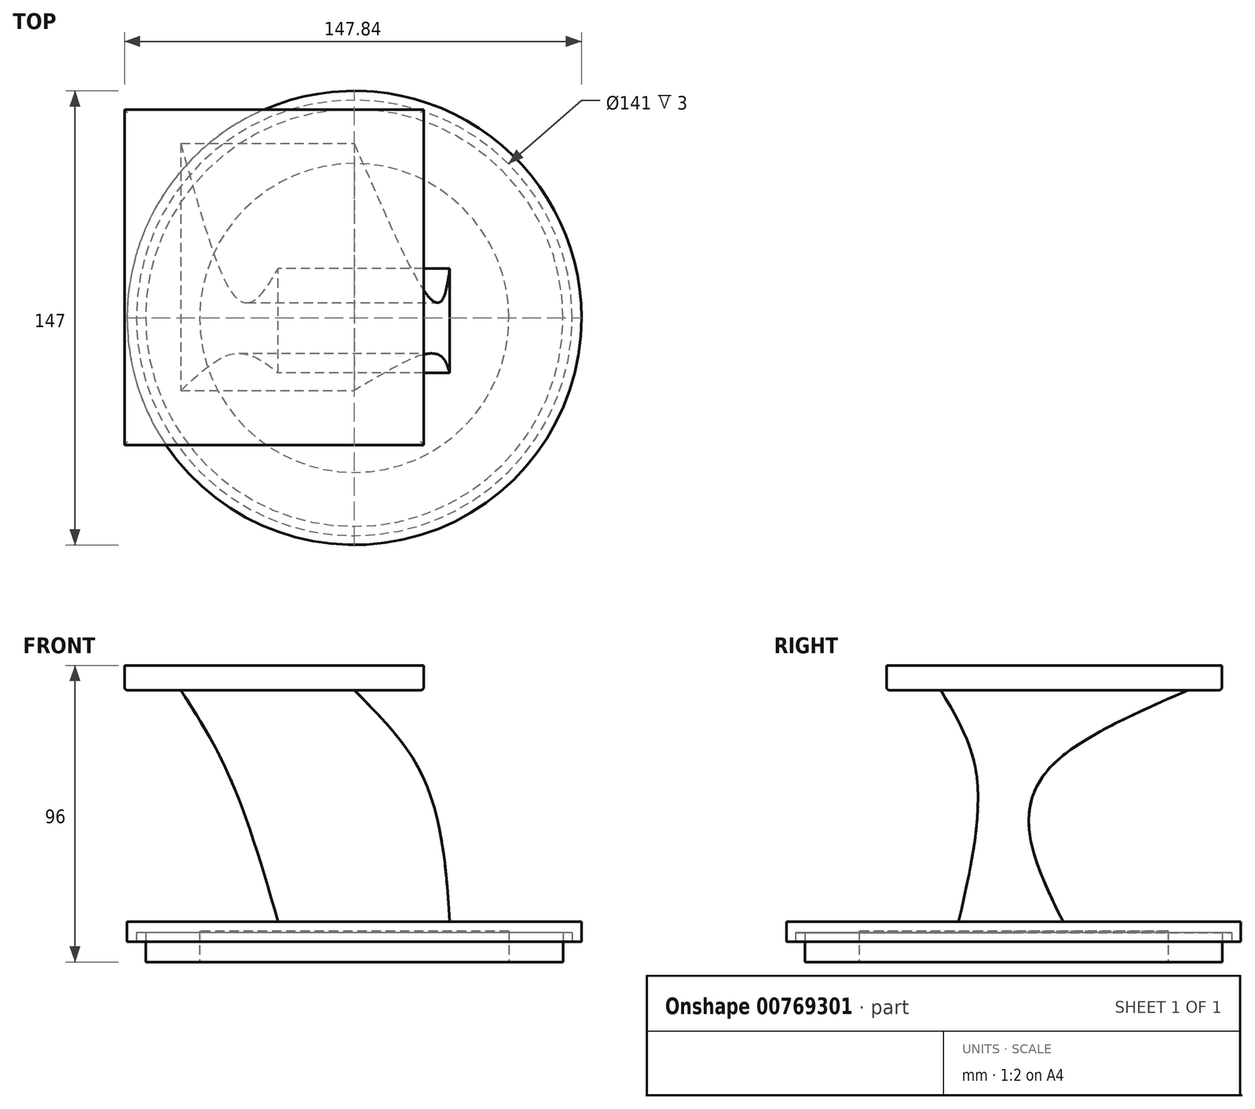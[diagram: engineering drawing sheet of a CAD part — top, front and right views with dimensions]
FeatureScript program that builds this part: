
annotation { "Feature Type Name" : "Feature", "Feature Type Description" : "" }
export const myFeature = defineFeature(function(context is Context, id is Id, definition is map)
    precondition{}
    {
        {
            var Q0;
            Q0=qCreatedBy(makeId("Top.planeOp"),FACE);
            var sketch = newSketch(context, id + "F0", { "sketchPlane" : qUnion([Q0])});
            skCircle(sketch, "E0", {"center": v(0, 0) * mm, "radius": 50 * mm});
            skCircle(sketch, "E1", {"center": v(0, 0) * mm, "radius": 67.5 * mm});
            skCircle(sketch, "E2", {"center": v(0, 0) * mm, "radius": 70.5 * mm});
            skCircle(sketch, "E3", {"center": v(0, 0) * mm, "radius": 73.5 * mm});
            skCircle(sketch, "E4", {"center": v(0, 0) * mm, "radius": 56.9 * mm, "construction": true});
            skPoint(sketch, "E5", {"position": v(56.9, 0) * mm});
            skPoint(sketch, "E6", {"position": v(67.5, 0) * mm});
            skPoint(sketch, "E7", {"position": v(70.5, 0) * mm});
            skPoint(sketch, "E8", {"position": v(73.5, 0) * mm});
            skLineSegment(sketch, "E9", {"start": v(0, 0) * mm, "end": v(0, 56.9) * mm, "construction": true});
            skLineSegment(sketch, "E10", {"start": v(0, 0) * mm, "end": v(-49.28, -28.45) * mm, "construction": true});
            skLineSegment(sketch, "E11", {"start": v(0, 0) * mm, "end": v(49.28, -28.45) * mm, "construction": true});
            skPoint(sketch, "E12", {"position": v(0, 56.9) * mm});
            skPoint(sketch, "E13", {"position": v(-49.28, -28.45) * mm});
            skPoint(sketch, "E14", {"position": v(49.28, -28.45) * mm});
            skPoint(sketch, "E15", {"position": v(0, 73.5) * mm});
            skLineSegment(sketch, "E16", {"start": v(-49.28, -28.45) * mm, "end": v(-63.47, -37.07) * mm, "construction": true});
            skPoint(sketch, "E17", {"position": v(-63.47, -37.07) * mm});
            skLineSegment(sketch, "E18", {"start": v(49.28, -28.45) * mm, "end": v(63.65, -36.75) * mm, "construction": true});
            skPoint(sketch, "E19", {"position": v(63.65, -36.75) * mm});
            skSolve(sketch);
        }
        {
            var Q0;
            Q0=makeQuery(id+"F0.imprint","IMPRINT",FACE,{"disambiguationData":[TD([[makeQuery(id+"F0.imprint","IMPRINT",EDGE,{"derivedFrom":sQuery(id+"F0.wireOp",EDGE,"E2")}),-1.0]])]});
            var Q1;
            Q1=makeQuery(id+"F0.imprint","IMPRINT",FACE,{"disambiguationData":[TD([[makeQuery(id+"F0.imprint","IMPRINT",EDGE,{"derivedFrom":sQuery(id+"F0.wireOp",EDGE,"E0")}),-1.0]])]});
            var Q2;
            Q2=makeQuery(id+"F0.imprint","IMPRINT",FACE,{"disambiguationData":[TD([[makeQuery(id+"F0.imprint","IMPRINT",EDGE,{"derivedFrom":sQuery(id+"F0.wireOp",EDGE,"E1")}),-1.0]])]});
            var Q3;
            Q3=makeQuery(id+"F0.imprint","IMPRINT",FACE,{"disambiguationData":[TD([[makeQuery(id+"F0.imprint","IMPRINT",EDGE,{"derivedFrom":sQuery(id+"F0.wireOp",EDGE,"E0")}),1.0]])]});
            extrude(context, id + "F1", {"entities" : qUnion([Q0, Q1, Q2, Q3]), "depth" : 13 * mm, "offsetDistance" : 25 * mm});
        }
        {
            var Q0;
            Q0=makeQuery(id+"F0.imprint","IMPRINT",FACE,{"disambiguationData":[TD([[makeQuery(id+"F0.imprint","IMPRINT",EDGE,{"derivedFrom":sQuery(id+"F0.wireOp",EDGE,"E0")}),1.0]])]});
            extrude(context, id + "F2", {"entities" : qUnion([Q0]), "operationType" : NewBodyOperationType.REMOVE, "depth" : 10 * mm, "offsetDistance" : 25 * mm});
        }
        {
            var Q0;
            Q0=makeQuery(id+"F0.imprint","IMPRINT",FACE,{"disambiguationData":[TD([[makeQuery(id+"F0.imprint","IMPRINT",EDGE,{"derivedFrom":sQuery(id+"F0.wireOp",EDGE,"E1")}),-1.0]])]});
            extrude(context, id + "F3", {"entities" : qUnion([Q0]), "operationType" : NewBodyOperationType.REMOVE, "depth" : 9.5 * mm, "offsetDistance" : 25 * mm});
        }
        {
            var Q0;
            Q0=makeQuery(id+"F0.imprint","IMPRINT",FACE,{"disambiguationData":[TD([[makeQuery(id+"F0.imprint","IMPRINT",EDGE,{"derivedFrom":sQuery(id+"F0.wireOp",EDGE,"E2")}),-1.0]])]});
            extrude(context, id + "F4", {"entities" : qUnion([Q0]), "operationType" : NewBodyOperationType.REMOVE, "depth" : 6.5 * mm, "offsetDistance" : 25 * mm});
        }
        {
            var Q0;
            Q0=makeQuery(id+"F1.opExtrude","CAP_FACE",FACE,{"disambiguationData":[OSD([sQuery(id+"F0.wireOp",EDGE,"E3")])],"isStart":false});
            var sketch = newSketch(context, id + "F5", { "sketchPlane" : qUnion([Q0])});
            skLineSegment(sketch, "E20.bottom", {"start": v(30.88, -17.82) * mm, "end": v(-24.6, -17.82) * mm});
            skLineSegment(sketch, "E20.top", {"start": v(30.88, 16.04) * mm, "end": v(-24.6, 16.04) * mm});
            skLineSegment(sketch, "E20.left", {"start": v(30.88, -17.82) * mm, "end": v(30.88, 16.04) * mm});
            skLineSegment(sketch, "E20.right", {"start": v(-24.6, -17.82) * mm, "end": v(-24.6, 16.04) * mm});
            skSolve(sketch);
        }
        {
            var Q0;
            Q0=makeQuery(id+"F5.imprint","IMPRINT",FACE,{"disambiguationData":[TD([[makeQuery(id+"F5.imprint","IMPRINT",EDGE,{"derivedFrom":sQuery(id+"F5.wireOp",EDGE,"E20.bottom")}),1.0]])]});
            cPlane(context, id + "F6", {"entities" : qUnion([Q0]), "cplaneType" : CPlaneType.OFFSET, "offset" : 25 * mm, "width" : 150 * mm, "height" : 150 * mm});
        }
        {
            var Q0;
            Q0=qCreatedBy(id+"F6.planeOp",FACE);
            cPlane(context, id + "F7", {"entities" : qUnion([Q0]), "cplaneType" : CPlaneType.OFFSET, "offset" : 25 * mm, "width" : 150 * mm, "height" : 150 * mm});
        }
        {
            var Q0;
            Q0=qCreatedBy(id+"F7.planeOp",FACE);
            cPlane(context, id + "F8", {"entities" : qUnion([Q0]), "cplaneType" : CPlaneType.OFFSET, "offset" : 25 * mm, "width" : 150 * mm, "height" : 150 * mm});
        }
        {
            var Q0;
            Q0=qCreatedBy(id+"F7.planeOp",FACE);
            var sketch = newSketch(context, id + "F9", { "sketchPlane" : qUnion([Q0])});
            skLineSegment(sketch, "E21.bottom", {"start": v(-41.72, 11.8) * mm, "end": v(20.67, 11.8) * mm});
            skLineSegment(sketch, "E21.top", {"start": v(-41.72, -12.4) * mm, "end": v(20.67, -12.4) * mm});
            skLineSegment(sketch, "E21.left", {"start": v(-41.72, 11.8) * mm, "end": v(-41.72, -12.4) * mm});
            skLineSegment(sketch, "E21.right", {"start": v(20.67, 11.8) * mm, "end": v(20.67, -12.4) * mm});
            skSolve(sketch);
        }
        {
            var Q0;
            Q0=qCreatedBy(id+"F8.planeOp",FACE);
            var sketch = newSketch(context, id + "F10", { "sketchPlane" : qUnion([Q0])});
            skLineSegment(sketch, "E22.bottom", {"start": v(-56.12, 56.47) * mm, "end": v(0, 56.47) * mm});
            skLineSegment(sketch, "E22.top", {"start": v(-56.12, -23.53) * mm, "end": v(0, -23.53) * mm});
            skLineSegment(sketch, "E22.left", {"start": v(-56.12, 56.47) * mm, "end": v(-56.12, -23.53) * mm});
            skLineSegment(sketch, "E22.right", {"start": v(0, 56.47) * mm, "end": v(0, -23.53) * mm});
            skSolve(sketch);
        }
        {
            var Q1;
            Q1=makeQuery(id+"F5.imprint","IMPRINT",FACE,{"disambiguationData":[TD([[makeQuery(id+"F5.imprint","IMPRINT",EDGE,{"derivedFrom":sQuery(id+"F5.wireOp",EDGE,"E20.bottom")}),-1.0]])]});
            var Q2;
            Q2=makeQuery(id+"F9.imprint","IMPRINT",FACE,{"disambiguationData":[TD([[makeQuery(id+"F9.imprint","IMPRINT",EDGE,{"derivedFrom":sQuery(id+"F9.wireOp",EDGE,"E21.bottom")}),-1.0]])]});
            var Q3;
            Q3=makeQuery(id+"F10.imprint","IMPRINT",FACE,{"disambiguationData":[TD([[makeQuery(id+"F10.imprint","IMPRINT",EDGE,{"derivedFrom":sQuery(id+"F10.wireOp",EDGE,"E22.bottom")}),-1.0]])]});
            loft(context, id + "F11", {"operationType" : NewBodyOperationType.ADD, "sheetProfilesArray" : [{ "sheetProfileEntities" : qUnion([Q1]) }, { "sheetProfileEntities" : qUnion([Q2]) }, { "sheetProfileEntities" : qUnion([Q3]) }]});
        }
        {
            var Q0;
            Q0=makeQuery(id+"F11.opLoft","CAP_FACE",FACE,{"disambiguationData":[OSD([makeQuery(id+"F10.imprint","IMPRINT",FACE,{"disambiguationData":[TD([[makeQuery(id+"F10.imprint","IMPRINT",EDGE,{"derivedFrom":sQuery(id+"F10.wireOp",EDGE,"E22.bottom")}),-1.0]])]})])],"isStart":true});
            var sketch = newSketch(context, id + "F12", { "sketchPlane" : qUnion([Q0])});
            skLineSegment(sketch, "E23.bottom", {"start": v(-74.34, 67.43) * mm, "end": v(22.48, 67.43) * mm});
            skLineSegment(sketch, "E23.top", {"start": v(-74.34, -41.12) * mm, "end": v(22.48, -41.12) * mm});
            skLineSegment(sketch, "E23.left", {"start": v(-74.34, 67.43) * mm, "end": v(-74.34, -41.12) * mm});
            skLineSegment(sketch, "E23.right", {"start": v(22.48, 67.43) * mm, "end": v(22.48, -41.12) * mm});
            skSolve(sketch);
        }
        {
            var Q0;
            Q0=makeQuery(id+"F12.imprint","IMPRINT",FACE,{"disambiguationData":[TD([[makeQuery(id+"F12.imprint","IMPRINT",EDGE,{"derivedFrom":sQuery(id+"F12.wireOp",EDGE,"E23.bottom")}),-1.0]])]});
            var Q1;
            {var subQ0=sQuery(id+"F10.wireOp",EDGE,"E22.right");var subQ1=sQuery(id+"F10.wireOp",EDGE,"E22.left");var subQ2=sQuery(id+"F10.wireOp",EDGE,"E22.bottom");Q1=makeQuery(id+"F12.imprint","IMPRINT",FACE,{"disambiguationData":[TD([[makeQuery(id+"F12.imprint","IMPRINT",EDGE,{"derivedFrom":makeQuery(id+"F11.opLoft","MID_CAP_EDGE",EDGE,{"disambiguationData":[OSD([subQ2,subQ1,subQ0])],"capPos":2.0})}),1.0]])]});}
            extrude(context, id + "F13", {"entities" : qUnion([Q0, Q1]), "depth" : 8 * mm, "offsetDistance" : 25 * mm});
        }
        {
            var Q0;
            Q0=makeQuery(id+"F13.opExtrude","CAP_FACE",FACE,{"disambiguationData":[OSD([sQuery(id+"F12.wireOp",EDGE,"E23.bottom"),sQuery(id+"F12.wireOp",EDGE,"E23.top"),sQuery(id+"F12.wireOp",EDGE,"E23.left"),sQuery(id+"F12.wireOp",EDGE,"E23.right")])],"isStart":true});
            fillet(context, id + "F14", {"entities" : qUnion([Q0]), "radius" : 1 * mm, "tangentPropagation" : true, "allowEdgeOverflow" : false});
        }
    });
